# Revit family: QF_ELECTROLUXPROFESSIONAL_535138_NMHABDR6M
name_source: partatom
category: Specialty Equipment
units: mm (PartAtom-declared; Revit-internal decimal feet)

## family parameters
Always vertical = Yes
Cut with Voids When Loaded = No
Enable Cutting in Views = No
Maintain Annotation Orientation = No
Part Type = Normal
Room Calculation Point = No
Round Connector Dimension = Use Diameter
Shared = No
Work Plane-Based = No

## types (2) — shared parameters
Accessory = No
Cold Water Size = 0 mm
Compressed Air Pressure = 0.0 Pa
Compressed Air Size = 0 mm
Compressed Air Volume = 0.0 L/s
Condensate Return Size = 0 mm
Cycle = 50 Hz
Depth Actual = 795 mm  [stored 2.60827 ft]
Description = MEDIUM DRYER WITHOUT DOOR (HAB), DUAL RINSE RT, ELECTRIC, 440/ 3/ 60Hz-MARINE
Direct Waste Size = 50 mm
Gas Input Pressure = 0
Gas Size = 0 mm
HP = 5.9 HP
Height Actual = 1130 mm  [stored 3.70735 ft]
Hot Water Size = 0 mm
Item Number = 535138
Length Actual = 560 mm  [stored 1.83727 ft]
Manufacturer = Electrolux Professional
Model = NMHABDR6M
Phase = 3
Refrigerant Compressor Remote = Yes
Refrigeration Liquid Line Size = 0 mm
Refrigeration Suction Line Size = 0 mm
Steam Supply Maximum Pressure = 0.0 Pa
Steam Supply Minimum Pressure = 0.0 Pa
Steam Supply Size = 0 mm
URL = http://www.electroluxprofessional.com
URL Manufacturer = http://www.electroluxprofessional.com
Volts = 440 V
Watts = 0 W
Weight = 52.00 kg
zero-valued in all types: Default Elevation, Gas KW, Steam Pounds per Hour

## type names (no varying parameters)
- NMHDRE56
- Standard

note: source unit labels omitted for Gas Input Pressure — the stored unit's dimension contradicts the parameter name (converter mislabeling)

note: [stored X ft] marks values corroborated as IEEE doubles in the binary element streams (Revit-internal decimal feet)
